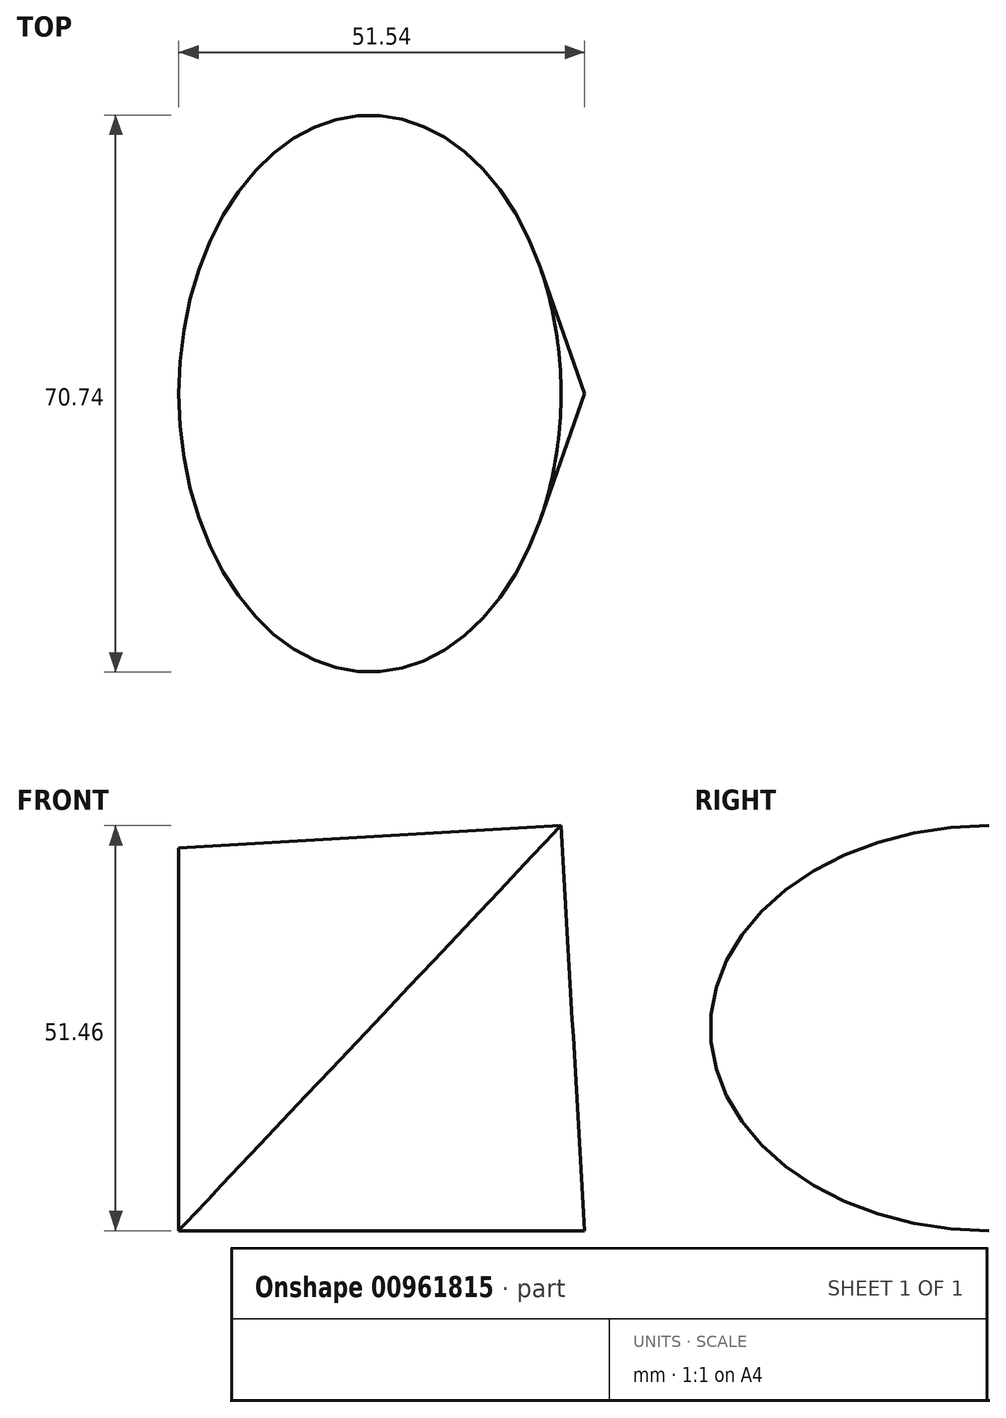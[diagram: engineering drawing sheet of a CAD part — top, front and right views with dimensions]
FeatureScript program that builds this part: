
annotation { "Feature Type Name" : "Feature", "Feature Type Description" : "" }
export const myFeature = defineFeature(function(context is Context, id is Id, definition is map)
    precondition{}
    {
        {
            var Q0;
            Q0=qCreatedBy(makeId("Front.planeOp"),FACE);
            var sketch = newSketch(context, id + "F0", { "sketchPlane" : qUnion([Q0])});
            skLineSegment(sketch, "E0", {"start": v(0, 0) * mm, "end": v(0, 48.62) * mm});
            skLineSegment(sketch, "E1", {"start": v(0, 48.62) * mm, "end": v(51.54, 0) * mm});
            skLineSegment(sketch, "E2", {"start": v(51.54, 0) * mm, "end": v(0, 0) * mm});
            skSolve(sketch);
        }
        {
            var Q0;
            Q0=makeQuery(id+"F0.imprint","IMPRINT",FACE,{"disambiguationData":[TD([[makeQuery(id+"F0.imprint","IMPRINT",EDGE,{"derivedFrom":sQuery(id+"F0.wireOp",EDGE,"E0")}),-1.0]])]});
            var Q1;
            Q1=sQuery(id+"F0.wireOp",EDGE,"E1");
            revolve(context, id + "F1", {"surfaceOperationType" : NewSurfaceOperationType.NEW, "entities" : qUnion([Q0]), "axis" : qUnion([Q1]), "revolveType" : RevolveType.FULL});
        }
    });
